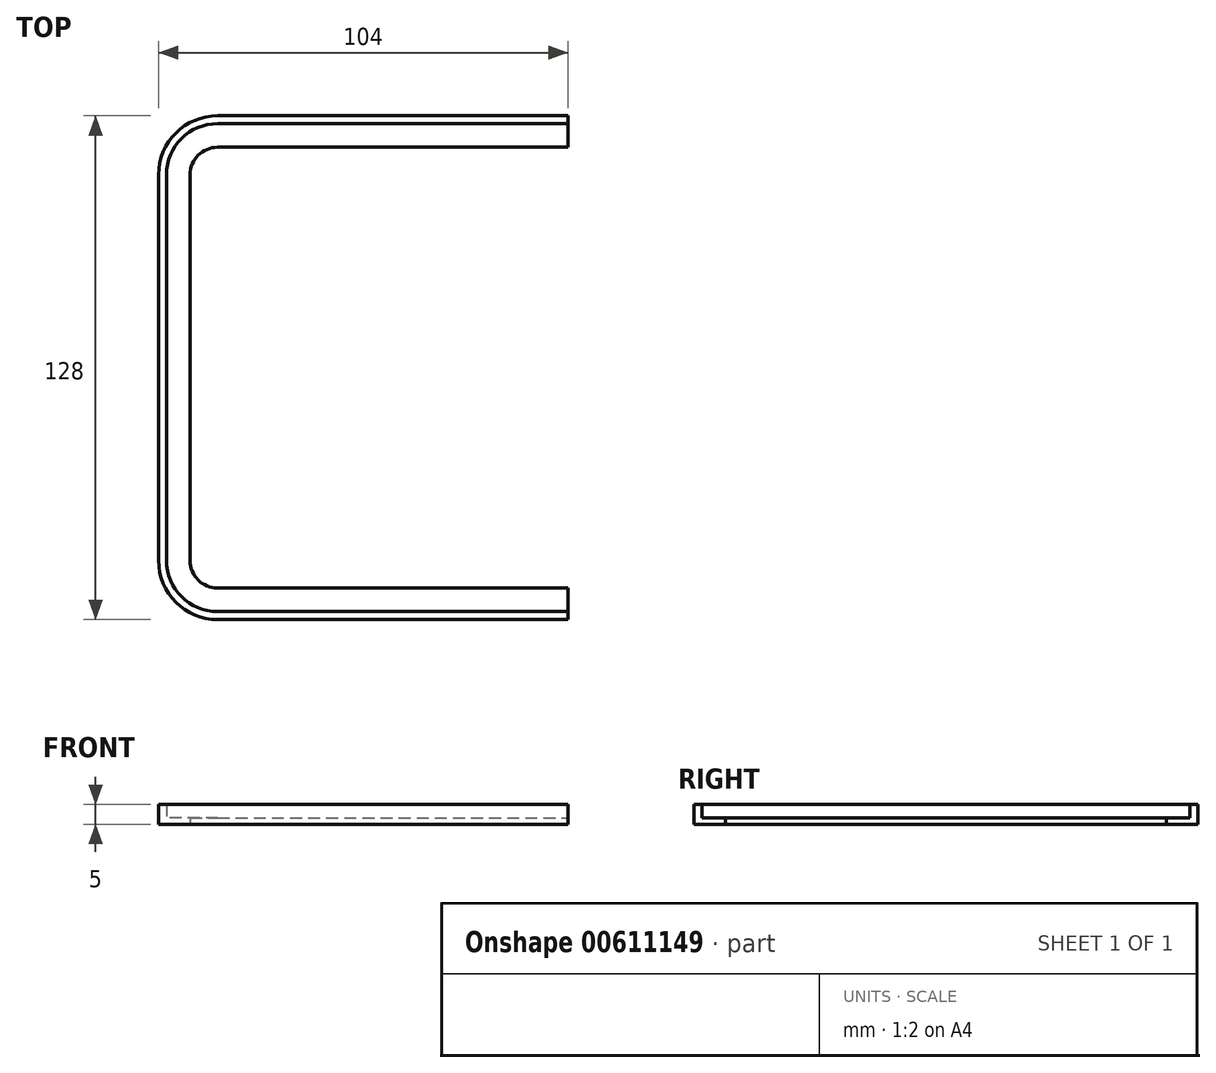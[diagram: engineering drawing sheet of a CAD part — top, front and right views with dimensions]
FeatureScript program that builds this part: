
annotation { "Feature Type Name" : "Feature", "Feature Type Description" : "" }
export const myFeature = defineFeature(function(context is Context, id is Id, definition is map)
    precondition{}
    {
        {
            var Q0;
            Q0=qCreatedBy(makeId("Top.planeOp"),FACE);
            var sketch = newSketch(context, id + "F0", { "sketchPlane" : qUnion([Q0])});
            skLineSegment(sketch, "E0.bottom", {"start": v(-38, 62) * mm, "end": v(51, 62) * mm});
            skLineSegment(sketch, "E0.top", {"start": v(-38, -62) * mm, "end": v(51, -62) * mm});
            skLineSegment(sketch, "E0.left", {"start": v(-51, 49) * mm, "end": v(-51, -49) * mm});
            skLineSegment(sketch, "E0.right", {"start": v(51, 62) * mm, "end": v(51, 56) * mm});
            skPoint(sketch, "E0.middle", {"position": v(0, 0) * mm});
            skPoint(sketch, "E1.visualSharp", {"position": v(-51, 62) * mm});
            skArc(sketch, "E1.filletArc", {"start": v(-38, 62) * mm, "mid": v(-47.2, 58.2) * mm, "end": v(-51, 49) * mm});
            skPoint(sketch, "E2.visualSharp", {"position": v(-51, -62) * mm});
            skArc(sketch, "E2.filletArc", {"start": v(-51, -49) * mm, "mid": v(-47.2, -58.2) * mm, "end": v(-38, -62) * mm});
            skLineSegment(sketch, "E3.0", {"start": v(-38, 56) * mm, "end": v(51, 56) * mm});
            skLineSegment(sketch, "E3.1", {"start": v(-38, -56) * mm, "end": v(51, -56) * mm});
            skArc(sketch, "E3.2", {"start": v(-45, -49) * mm, "mid": v(-42.95, -53.95) * mm, "end": v(-38, -56) * mm});
            skLineSegment(sketch, "E3.3", {"start": v(-45, 49) * mm, "end": v(-45, -49) * mm});
            skArc(sketch, "E3.4", {"start": v(-38, 56) * mm, "mid": v(-42.95, 53.95) * mm, "end": v(-45, 49) * mm});
            skLineSegment(sketch, "E4.trimOffspring", {"start": v(51, -56) * mm, "end": v(51, -62) * mm});
            skLineSegment(sketch, "E5.0", {"start": v(-38, 64) * mm, "end": v(51, 64) * mm});
            skLineSegment(sketch, "E5.1", {"start": v(-38, -64) * mm, "end": v(51, -64) * mm});
            skArc(sketch, "E5.2", {"start": v(-53, -49) * mm, "mid": v(-48.6, -59.6) * mm, "end": v(-38, -64) * mm});
            skLineSegment(sketch, "E5.3", {"start": v(-53, 49) * mm, "end": v(-53, -49) * mm});
            skArc(sketch, "E5.4", {"start": v(-38, 64) * mm, "mid": v(-48.6, 59.6) * mm, "end": v(-53, 49) * mm});
            skLineSegment(sketch, "E6", {"start": v(51, -62) * mm, "end": v(51, -64) * mm});
            skLineSegment(sketch, "E7", {"start": v(51, 64) * mm, "end": v(51, 62) * mm});
            skSolve(sketch);
        }
        {
            var Q0;
            Q0=makeQuery(id+"F0.imprint","IMPRINT",FACE,{"disambiguationData":[TD([[makeQuery(id+"F0.imprint","IMPRINT",EDGE,{"derivedFrom":sQuery(id+"F0.wireOp",EDGE,"E0.bottom")}),-1.0]])]});
            extrude(context, id + "F1", {"entities" : qUnion([Q0]), "depth" : 1.6 * mm, "offsetDistance" : 25 * mm});
        }
        {
            var Q0;
            Q0=makeQuery(id+"F0.imprint","IMPRINT",FACE,{"disambiguationData":[TD([[makeQuery(id+"F0.imprint","IMPRINT",EDGE,{"derivedFrom":sQuery(id+"F0.wireOp",EDGE,"E0.bottom")}),1.0]])]});
            extrude(context, id + "F2", {"entities" : qUnion([Q0]), "operationType" : NewBodyOperationType.ADD, "depth" : 5 * mm, "offsetDistance" : 25 * mm});
        }
    });
